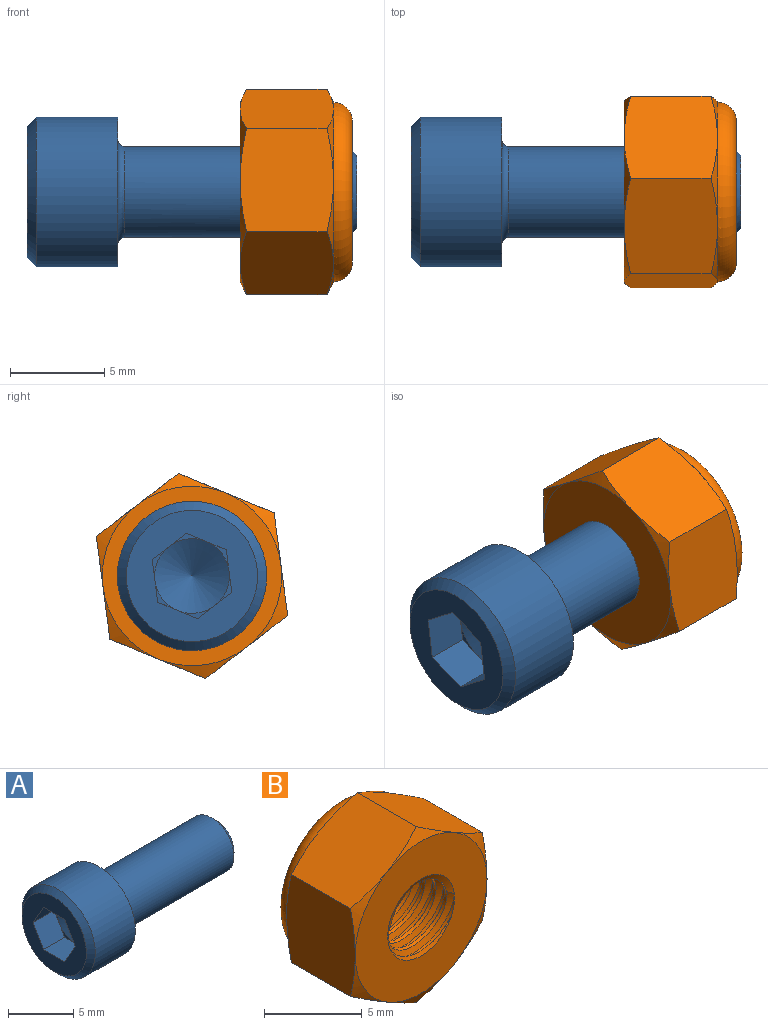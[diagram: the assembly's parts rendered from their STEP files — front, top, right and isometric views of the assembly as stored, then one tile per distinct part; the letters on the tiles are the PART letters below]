
ASSEMBLY  parts=2 mates=2
PART A: 21 faces, bbox 17.5x7.9x7.9 mm
  f0: cone r=1.99mm half-angle=60deg, axis (-1,0,0), area 14.3mm2, adj f15,f16,f17,f18,f19,f20
  f1: torus R=2.77mm, axis (1,0,0), area 8.9mm2, adj f3,f7
  f2: cone r=1.94mm half-angle=45deg, axis (-1,0,0), area 9.1mm2, adj f3,f8
  f3: cylinder r=2.41mm len=11.87mm, axis (-1,0,0), area 180mm2, adj f1,f2
  f4: cylinder r=3.97mm len=7.94mm, axis (-1,0,0), area 108.3mm2, adj f5,f7
  f5: cone r=3.49mm half-angle=45deg, axis (1,0,0), area 16mm2, adj f4,f6
  f6: plane 6.97x6.97mm, normal (-1,0,0), area 24.5mm2, adj f5,f9,f10,f11,f12,f13,f14
  f7: plane 7.94x7.94mm, normal (1,0,0), area 25.4mm2, adj f1,f4
  f8: plane 3.88x3.88mm, normal (1,0,0), area 11.8mm2, adj f2
  f9: plane 2.29x1.99mm, normal (0,-0.87,-0.5), area 5.2mm2, adj f6,f10,f14,f19,f20
  f10: plane 2.29x2.29mm, normal (0,0,-1), area 5.2mm2, adj f6,f9,f11,f15,f20
  f11: plane 2.29x1.99mm, normal (0,0.87,-0.5), area 5.2mm2, adj f6,f10,f12,f15,f16
  f12: plane 2.29x1.99mm, normal (0,0.87,0.5), area 5.2mm2, adj f6,f11,f13,f16,f17
  f13: plane 2.29x2.29mm, normal (0,0,1), area 5.2mm2, adj f6,f12,f14,f17,f18
  f14: plane 2.29x1.99mm, normal (0,-0.87,0.5), area 5.2mm2, adj f6,f9,f13,f18,f19
  f15: plane 1.72x0.99mm, normal (-1,0,0), area 0.2mm2, adj f0,f10,f11
  f16: plane 1.99x0.57mm, normal (-1,0,0), area 0.2mm2, adj f0,f11,f12
  f17: plane 1.72x0.99mm, normal (-1,0,0), area 0.2mm2, adj f0,f12,f13
  f18: plane 1.72x0.99mm, normal (-1,0,0), area 0.2mm2, adj f0,f13,f14
  f19: plane 1.99x0.57mm, normal (-1,0,0), area 0.2mm2, adj f0,f9,f14
  f20: plane 1.72x0.99mm, normal (-1,0,0), area 0.2mm2, adj f0,f9,f10
PART B: 56 faces, bbox 11.4x6.5x11.4 mm
  f0: cylinder r=2.91mm len=5.82mm, axis (0,-1,0), area 2.8mm2, adj f31,f55
  f1: torus R=3.77mm, axis (0,-1,0), area 35.7mm2, adj f54,f55
  f2: torus R=3.77mm, axis (0,-1,0), area 43.1mm2, adj f3,f31,f43,f44,f45,f46,f47
  f3: cone r=4.76mm half-angle=65deg, axis (0,-1,0), area 2.1mm2, adj f2,f52,f53
  f4: cone r=5.5mm half-angle=65deg, axis (0,1,0), area 2.1mm2, adj f33,f49,f50
  f5: cylinder r=2.09mm len=4.18mm, axis (0,0.99,0.16), area 2.6mm2, adj f6,f7
  f6: cone r=2.09mm half-angle=60deg, axis (0,-0.99,-0.16), area 5.9mm2, adj f5,f26
  f7: cone r=2.52mm half-angle=60deg, axis (0,0.99,0.16), area 5.9mm2, adj f5,f25
  f8: cylinder r=2.09mm len=4.18mm, axis (0,0.99,0.16), area 2.6mm2, adj f9,f10
  f9: cone r=2.09mm half-angle=60deg, axis (0,-0.99,-0.16), area 5.9mm2, adj f8,f25
  f10: cone r=2.52mm half-angle=60deg, axis (0,0.99,0.16), area 5.9mm2, adj f8,f24
  f11: cylinder r=2.09mm len=4.18mm, axis (0,0.99,0.16), area 2.6mm2, adj f12,f13
  f12: cone r=2.09mm half-angle=60deg, axis (0,-0.99,-0.16), area 5.9mm2, adj f11,f24
  f13: cone r=2.52mm half-angle=60deg, axis (0,0.99,0.16), area 5.9mm2, adj f11,f23
  f14: cylinder r=2.09mm len=4.18mm, axis (0,0.99,0.16), area 2.6mm2, adj f15,f16
  f15: cone r=2.09mm half-angle=60deg, axis (0,-0.99,-0.16), area 5.9mm2, adj f14,f23
  f16: cone r=2.52mm half-angle=60deg, axis (0,0.99,0.16), area 5.9mm2, adj f14,f22
  f17: cylinder r=2.09mm len=4.18mm, axis (0,0.99,0.16), area 2.6mm2, adj f18,f19
  f18: cone r=2.09mm half-angle=60deg, axis (0,-0.99,-0.16), area 5.9mm2, adj f17,f22
  f19: cone r=2.52mm half-angle=60deg, axis (0,0.99,0.16), area 5.7mm2, adj f17,f36,f54
  f20: cylinder r=2.09mm len=4.14mm, axis (0,0.99,0.16), area 0.9mm2, adj f21,f37,f54
  f21: cone r=2.52mm half-angle=60deg, axis (0,0.99,0.16), area 0.5mm2, adj f20,f54
  f22: cylinder r=2.41mm len=4.83mm, axis (0,-1,0), area 2.9mm2, adj f16,f18
  f23: cylinder r=2.41mm len=4.83mm, axis (0,-1,0), area 2.9mm2, adj f13,f15
  f24: cylinder r=2.41mm len=4.83mm, axis (0,-1,0), area 2.9mm2, adj f10,f12
  f25: cylinder r=2.41mm len=4.83mm, axis (0,-1,0), area 2.9mm2, adj f7,f9
  f26: cylinder r=2.41mm len=4.83mm, axis (0,-1,0), area 2.9mm2, adj f6,f29
  f27: cylinder r=2.41mm len=4.83mm, axis (0,-1,0), area 1mm2, adj f28,f33,f35
  f28: cone r=2.09mm half-angle=60deg, axis (0,-0.99,-0.16), area 3mm2, adj f27,f32,f34
  f29: cone r=2.52mm half-angle=60deg, axis (0,0.99,0.16), area 5.9mm2, adj f26,f32,f34
  f30: cone r=2.41mm half-angle=65deg, axis (0,-1,0), area 0.7mm2, adj f33,f35
  f31: plane 7.54x7.54mm, normal (0,1,0), area 18.1mm2, adj f0,f2
  f32: cone r=2.41mm half-angle=65deg, axis (0,-1,0), area 2.2mm2, adj f28,f29,f33,f34
  f33: plane 9.53x9.53mm, normal (0,-1,0), area 53mm2, adj f4,f27,f30,f32,f38,f39,f40,f41
  f34: cylinder r=2.09mm len=4.18mm, axis (0,0.99,0.16), area 1.8mm2, adj f28,f29,f32
  f35: cone r=2.52mm half-angle=60deg, axis (0,0.99,0.16), area 0.8mm2, adj f27,f30
  f36: cylinder r=2.41mm len=4.83mm, axis (0,-1,0), area 4.7mm2, adj f19,f37,f54
  f37: cone r=2.09mm half-angle=60deg, axis (0,-0.99,-0.16), area 2.7mm2, adj f20,f36,f54
  f38: cone r=5.5mm half-angle=65deg, axis (0,1,0), area 2.1mm2, adj f33,f48,f49
  f39: cone r=5.5mm half-angle=65deg, axis (0,1,0), area 2.1mm2, adj f33,f48,f53
  f40: cone r=5.5mm half-angle=65deg, axis (0,1,0), area 2.1mm2, adj f33,f52,f53
  f41: cone r=5.5mm half-angle=65deg, axis (0,1,0), area 2.1mm2, adj f33,f51,f52
  f42: cone r=5.5mm half-angle=65deg, axis (0,1,0), area 2.1mm2, adj f33,f50,f51
  f43: cone r=4.76mm half-angle=65deg, axis (0,-1,0), area 2.1mm2, adj f2,f50,f51
  f44: cone r=4.76mm half-angle=65deg, axis (0,-1,0), area 2.1mm2, adj f2,f51,f52
  f45: cone r=4.76mm half-angle=65deg, axis (0,-1,0), area 2.1mm2, adj f2,f49,f50
  f46: cone r=4.76mm half-angle=65deg, axis (0,-1,0), area 2.1mm2, adj f2,f48,f53
  f47: cone r=4.76mm half-angle=65deg, axis (0,-1,0), area 2.1mm2, adj f2,f48,f49
  f48: plane 5.93x5.39mm, normal (1,0,0), area 26mm2, adj f38,f39,f46,f47,f49,f53
  f49: plane 5.39x5.19mm, normal (0.5,0,0.87), area 26mm2, adj f4,f38,f45,f47,f48,f50
  f50: plane 5.39x5.19mm, normal (-0.5,0,0.87), area 26mm2, adj f4,f42,f43,f45,f49,f51
  f51: plane 5.93x5.39mm, normal (-1,0,0), area 26mm2, adj f41,f42,f43,f44,f50,f52
  f52: plane 5.39x5.19mm, normal (-0.5,0,-0.87), area 26mm2, adj f3,f40,f41,f44,f51,f53
  f53: plane 5.39x5.19mm, normal (0.5,0,-0.87), area 26mm2, adj f3,f39,f40,f46,f48,f52
  f54: plane 9.36x9.36mm, normal (0,1,0), area 50.6mm2, adj f1,f19,f20,f21,f36,f37
  f55: plane 7.54x7.54mm, normal (0,-1,0), area 18.1mm2, adj f0,f1
PLACE A rot(axis=(1,0,0),22.4deg) t=(-11.83,3.53,3.65)mm
PLACE B rot(axis=(0.64,0.64,-0.43),133.7deg) t=(-0.51,3.53,3.65)mm
MATE planar B.f22 <-> A.f0  axis (1,0,0) through (5.44,3.53,3.65)mm
MATE cylindrical A.f0 <-> B.f22  axis (1,0,0) through (5.69,3.53,3.65)mm
